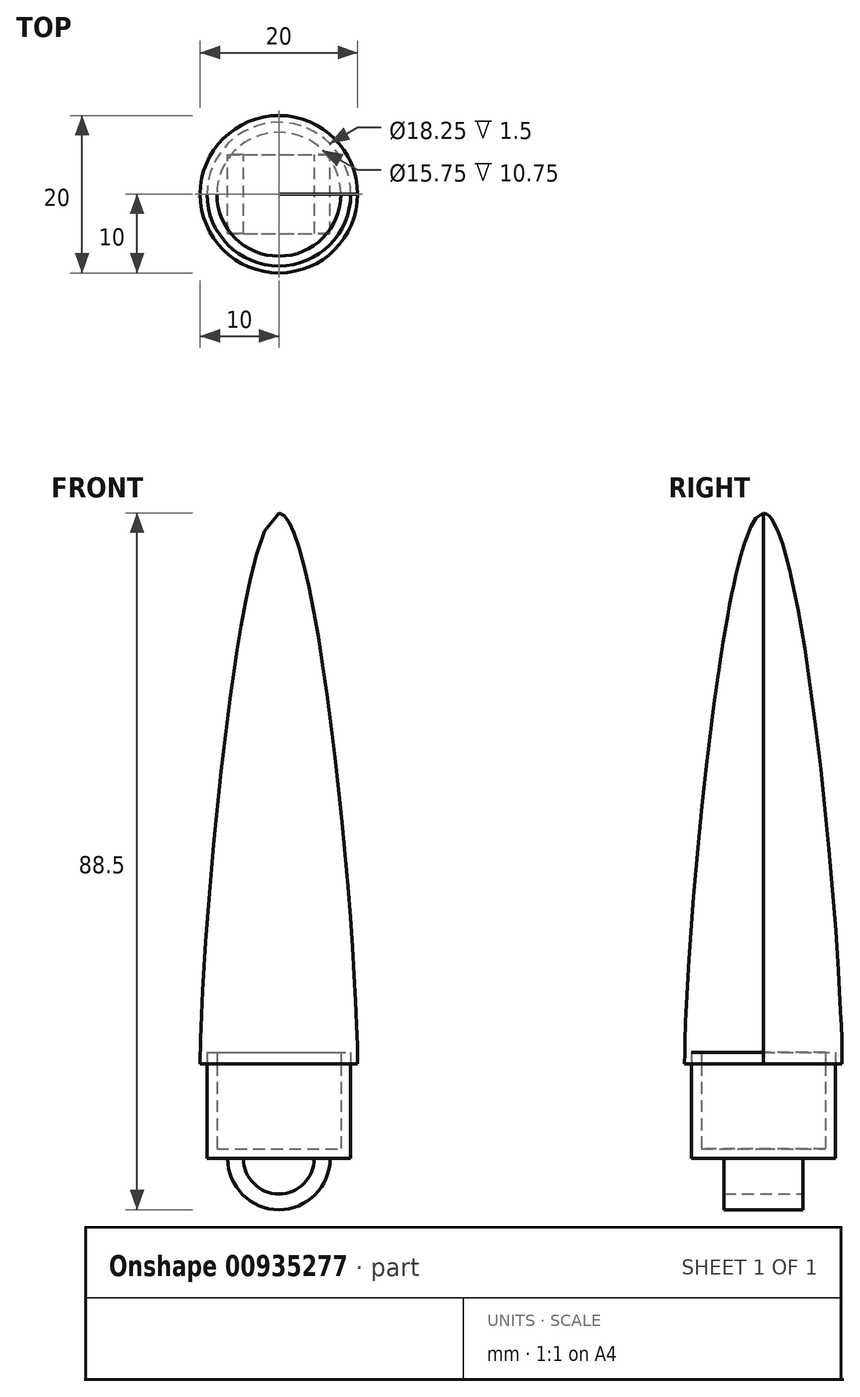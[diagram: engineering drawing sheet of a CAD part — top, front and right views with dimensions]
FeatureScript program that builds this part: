
annotation { "Feature Type Name" : "Feature", "Feature Type Description" : "" }
export const myFeature = defineFeature(function(context is Context, id is Id, definition is map)
    precondition{}
    {
        {
            var Q0;
            Q0=qCreatedBy(makeId("Front.planeOp"),FACE);
            var sketch = newSketch(context, id + "F0", { "sketchPlane" : qUnion([Q0])});
            skLineSegment(sketch, "E0", {"start": v(0, 0) * mm, "end": v(0, 70) * mm});
            skLineSegment(sketch, "E1", {"start": v(0, 0) * mm, "end": v(10, 0) * mm});
            skFitSpline(sketch, "E2", {"points": [v(0, 70) * mm, v(10, 0) * mm], "startDerivative": vector(15, 0) * mm, "endDerivative": vector(0, -48) * mm});
            skFitSpline(sketch, "E3.0", {"points": [v(-0.5, 68.7) * mm, v(-0.49, 68.7) * mm, v(-0.46, 68.67) * mm, v(-0.42, 68.64) * mm, v(-0.4, 68.62) * mm, v(-0.38, 68.61) * mm, v(-0.37, 68.6) * mm, v(-0.37, 68.6) * mm, v(-0.36, 68.6) * mm, v(-0.36, 68.6) * mm, v(-0.36, 68.6) * mm, v(-0.36, 68.6) * mm, v(-0.36, 68.6) * mm, v(-0.36, 68.6) * mm, v(-0.35, 68.58) * mm, v(-0.32, 68.56) * mm, v(-0.28, 68.52) * mm, v(-0.22, 68.44) * mm, v(-0.13, 68.3) * mm, v(0.01, 68.08) * mm, v(0.2, 67.72) * mm, v(0.46, 67.15) * mm, v(0.8, 66.25) * mm, v(1.22, 64.93) * mm, v(1.65, 63.38) * mm, v(2.07, 61.62) * mm, v(2.63, 59.04) * mm, v(3.32, 55.39) * mm, v(4.1, 50.48) * mm, v(4.85, 45.16) * mm, v(5.55, 39.57) * mm, v(6.19, 33.82) * mm, v(6.96, 26.12) * mm, v(7.75, 16.74) * mm, v(8.35, 6.88) * mm, v(8.5, 1.9) * mm, v(8.5, 0) * mm]});
            skLineSegment(sketch, "E4.bottom", {"start": v(7.88, 1.5) * mm, "end": v(9.12, 1.5) * mm});
            skLineSegment(sketch, "E4.top", {"start": v(7.88, -12) * mm, "end": v(9.12, -12) * mm});
            skLineSegment(sketch, "E4.left", {"start": v(7.88, 1.5) * mm, "end": v(7.88, -12) * mm});
            skLineSegment(sketch, "E4.right", {"start": v(9.12, 1.5) * mm, "end": v(9.12, -12) * mm});
            skLineSegment(sketch, "E5.bottom", {"start": v(7.88, -12) * mm, "end": v(0, -12) * mm});
            skLineSegment(sketch, "E5.top", {"start": v(7.88, -10.75) * mm, "end": v(0, -10.75) * mm});
            skLineSegment(sketch, "E5.left", {"start": v(7.88, -12) * mm, "end": v(7.88, -10.75) * mm});
            skLineSegment(sketch, "E5.right", {"start": v(0, -12) * mm, "end": v(0, -10.75) * mm});
            skSolve(sketch);
        }
        {
            var Q0;
            {var subQ5=sQuery(id+"F0.wireOp",EDGE,"E2");Q0=makeQuery(id+"F0.imprint","IMPRINT",FACE,{"disambiguationData":[TD([[makeQuery(id+"F0.imprint","IMPRINT",EDGE,{"derivedFrom":subQ5}),-1.0]])]});}
            var Q1;
            {var subQ0=sQuery(id+"F0.wireOp",EDGE,"E4.top");Q1=makeQuery(id+"F0.imprint","IMPRINT",FACE,{"disambiguationData":[TD([[makeQuery(id+"F0.imprint","IMPRINT",EDGE,{"derivedFrom":subQ0}),1.0]])]});}
            var Q2;
            {var subQ0=sQuery(id+"F0.wireOp",EDGE,"E3.0");var subQ1=sQuery(id+"F0.wireOp",EDGE,"E1");var subQ2=makeQuery(id+"F0.imprint","INTERSECT",VERTEX,{"derivedFrom":[subQ1,subQ0]});Q2=makeQuery(id+"F0.imprint","IMPRINT",FACE,{"disambiguationData":[TD([[makeQuery(id+"F0.imprint","IMPRINT",EDGE,{"disambiguationData":[TD([[subQ2,1.0]])],"derivedFrom":subQ1}),1.0]])]});}
            var Q3;
            {var subQ0=sQuery(id+"F0.wireOp",EDGE,"E3.0");var subQ1=sQuery(id+"F0.wireOp",EDGE,"E1");var subQ2=makeQuery(id+"F0.imprint","INTERSECT",VERTEX,{"derivedFrom":[subQ1,subQ0]});Q3=makeQuery(id+"F0.imprint","IMPRINT",FACE,{"disambiguationData":[TD([[makeQuery(id+"F0.imprint","IMPRINT",EDGE,{"disambiguationData":[TD([[subQ2,-1.0]])],"derivedFrom":subQ1}),1.0]])]});}
            var Q4;
            {var subQ5=sQuery(id+"F0.wireOp",EDGE,"E0");var subQ7=sQuery(id+"F0.wireOp",EDGE,"E1");var subQ8=makeQuery(id+"F0.imprint","INTERSECT",VERTEX,{"derivedFrom":[subQ5,subQ7]});Q4=makeQuery(id+"F0.imprint","IMPRINT",FACE,{"disambiguationData":[TD([[makeQuery(id+"F0.imprint","IMPRINT",EDGE,{"disambiguationData":[TD([[subQ8,-1.0]])],"derivedFrom":subQ5}),-1.0]])]});}
            var Q5;
            Q5=makeQuery(id+"F0.imprint","IMPRINT",FACE,{"disambiguationData":[TD([[makeQuery(id+"F0.imprint","IMPRINT",EDGE,{"derivedFrom":sQuery(id+"F0.wireOp",EDGE,"E5.bottom")}),-1.0]])]});
            var Q6;
            Q6=sQuery(id+"F0.wireOp",EDGE,"E0");
            revolve(context, id + "F1", {"surfaceOperationType" : NewSurfaceOperationType.NEW, "entities" : qUnion([Q0, Q1, Q2, Q3, Q4, Q5]), "axis" : qUnion([Q6]), "revolveType" : RevolveType.FULL});
        }
        {
            var Q0;
            Q0=qCreatedBy(makeId("Front.planeOp"),FACE);
            var sketch = newSketch(context, id + "F2", { "sketchPlane" : qUnion([Q0])});
            skLineSegment(sketch, "E6.0", {"start": v(9.12, -12) * mm, "end": v(-9.12, -12) * mm});
            skArc(sketch, "E7", {"start": v(-4.5, -12) * mm, "mid": v(0, -16.5) * mm, "end": v(4.5, -12) * mm});
            skArc(sketch, "E8.0", {"start": v(-6.5, -12) * mm, "mid": v(0, -18.5) * mm, "end": v(6.5, -12) * mm});
            skSolve(sketch);
        }
        {
            var Q0;
            {var subQ0=sQuery(id+"F2.wireOp",EDGE,"E7");Q0=makeQuery(id+"F2.imprint","IMPRINT",FACE,{"disambiguationData":[TD([[makeQuery(id+"F2.imprint","IMPRINT",EDGE,{"derivedFrom":subQ0}),-1.0]])]});}
            extrude(context, id + "F3", {"entities" : qUnion([Q0]), "operationType" : NewBodyOperationType.ADD, "depth" : 5 * mm, "offsetDistance" : 25 * mm, "hasSecondDirection" : true, "secondDirectionOppositeDirection" : true, "secondDirectionDepth" : 5 * mm});
        }
    });
